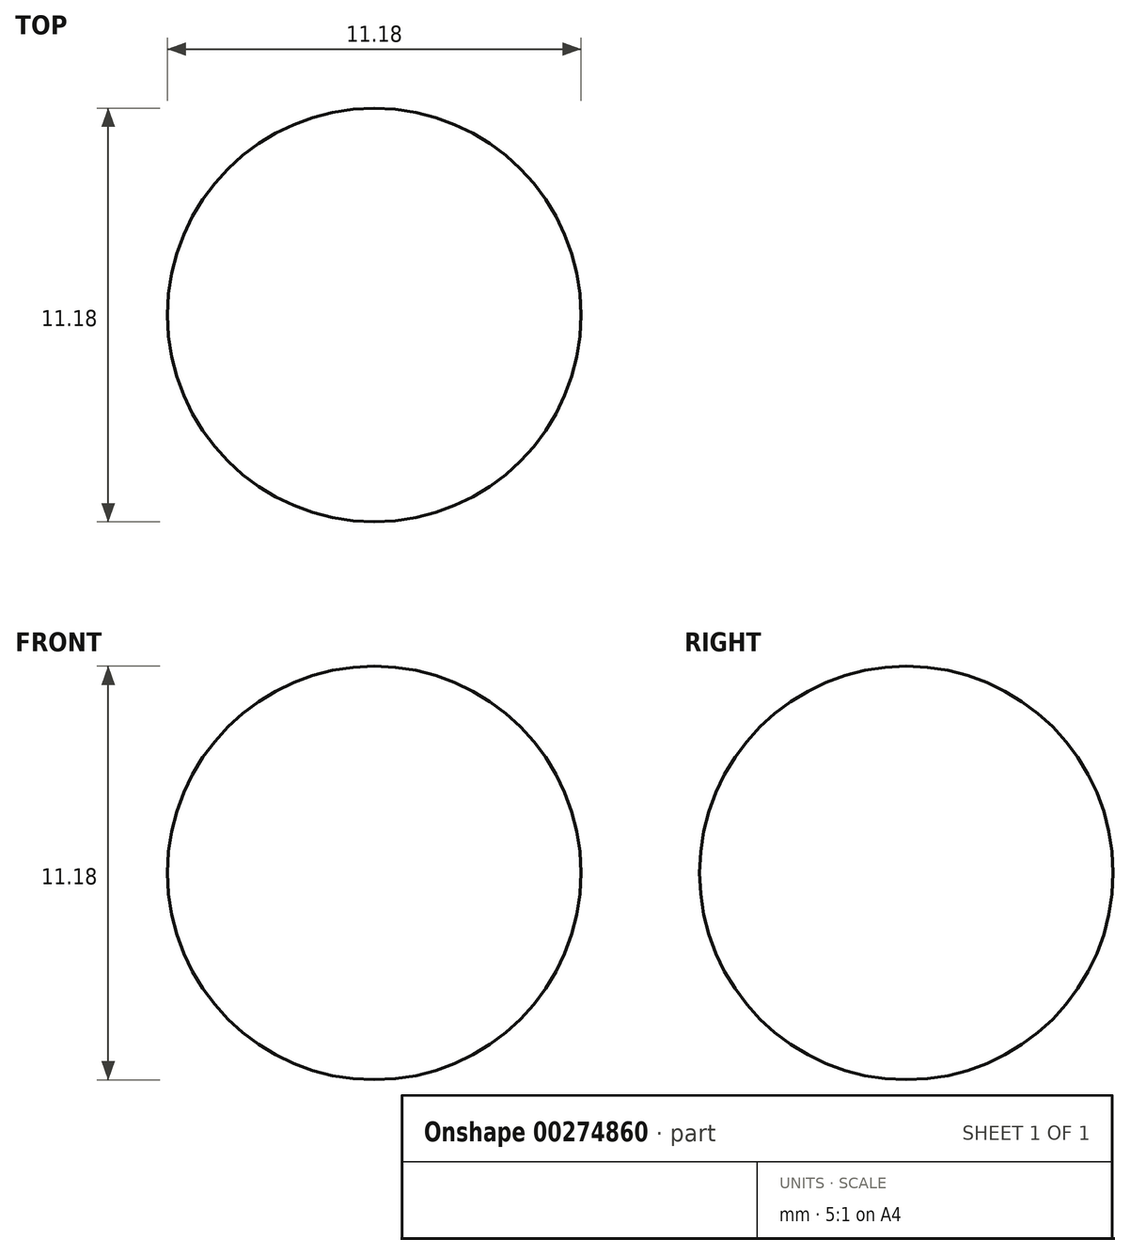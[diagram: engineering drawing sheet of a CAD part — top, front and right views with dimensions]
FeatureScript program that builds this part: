
annotation { "Feature Type Name" : "Feature", "Feature Type Description" : "" }
export const myFeature = defineFeature(function(context is Context, id is Id, definition is map)
    precondition{}
    {
        {
            var Q0;
            Q0=qCreatedBy(makeId("Top.planeOp"),FACE);
            var sketch = newSketch(context, id + "F0", { "sketchPlane" : qUnion([Q0])});
            skCircle(sketch, "E0", {"center": v(0, 0) * mm, "radius": 5.59 * mm});
            skLineSegment(sketch, "E1", {"start": v(0, 5.59) * mm, "end": v(0, -5.59) * mm});
            skSolve(sketch);
        }
        {
            var Q0;
            {var subQ0=sQuery(id+"F0.wireOp",EDGE,"E1");Q0=makeQuery(id+"F0.imprint","IMPRINT",FACE,{"disambiguationData":[TD([[makeQuery(id+"F0.imprint","IMPRINT",EDGE,{"derivedFrom":subQ0}),-1.0]])]});}
            var Q1;
            Q1=sQuery(id+"F0.wireOp",EDGE,"E1");
            revolve(context, id + "F1", {"entities" : qUnion([Q0]), "axis" : qUnion([Q1]), "revolveType" : RevolveType.FULL});
        }
    });
